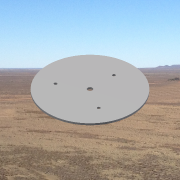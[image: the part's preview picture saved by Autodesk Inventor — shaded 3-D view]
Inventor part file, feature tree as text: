
AUTODESK INVENTOR PART (.ipt)
format: ipt  version: 2016 (Build 200138000, 138)  size: 142,848 bytes
history: native  units: in
note: dims shown in document units (in); Inventor stores cm internally (conversion verified against a paired STEP export)
features: sketch x3, hole x2, extrude x1
ambient origin geometry x8: Origin, YZ Plane, XZ Plane, XY Plane, X Axis, Y Axis, Z Axis, Center Point
bodies: Solid1 (feature_tree)
feature tree (6):
  extrude  "Extrusion1"  Depth=0.1575in TaperAngle=0.0deg
  hole  "Hole1"  [1 undecoded]
  hole  "Hole3"  [1 undecoded]
  sketch  "Sketch1"  dims[d0=7.874in d1=0.1575in d2=0.0in]
  sketch  "Sketch2"  dims[d3=0.3937in]
  sketch  "Sketch4"  dims[d4=0.4331in d5=0.75in d6=0.375in d7=0.25in d8=0.5635in d9=1.0in d10=0.8108in d24=0.25in d26=1.1811in d28=360.0deg d30=0.2598in d31=0.75in d32=0.375in d33=0.25in d34=0.5635in d35=1.0in d36=0.8108in d37=2.2441in d38=2.2441in d39=30.0deg d40=2.3622in d41=150.0deg]
note: 2 required parameter values undecoded (feature->parameter linkage not recoverable at this tier; creation-order binding heuristic only, values carry confidence <= 0.55)
